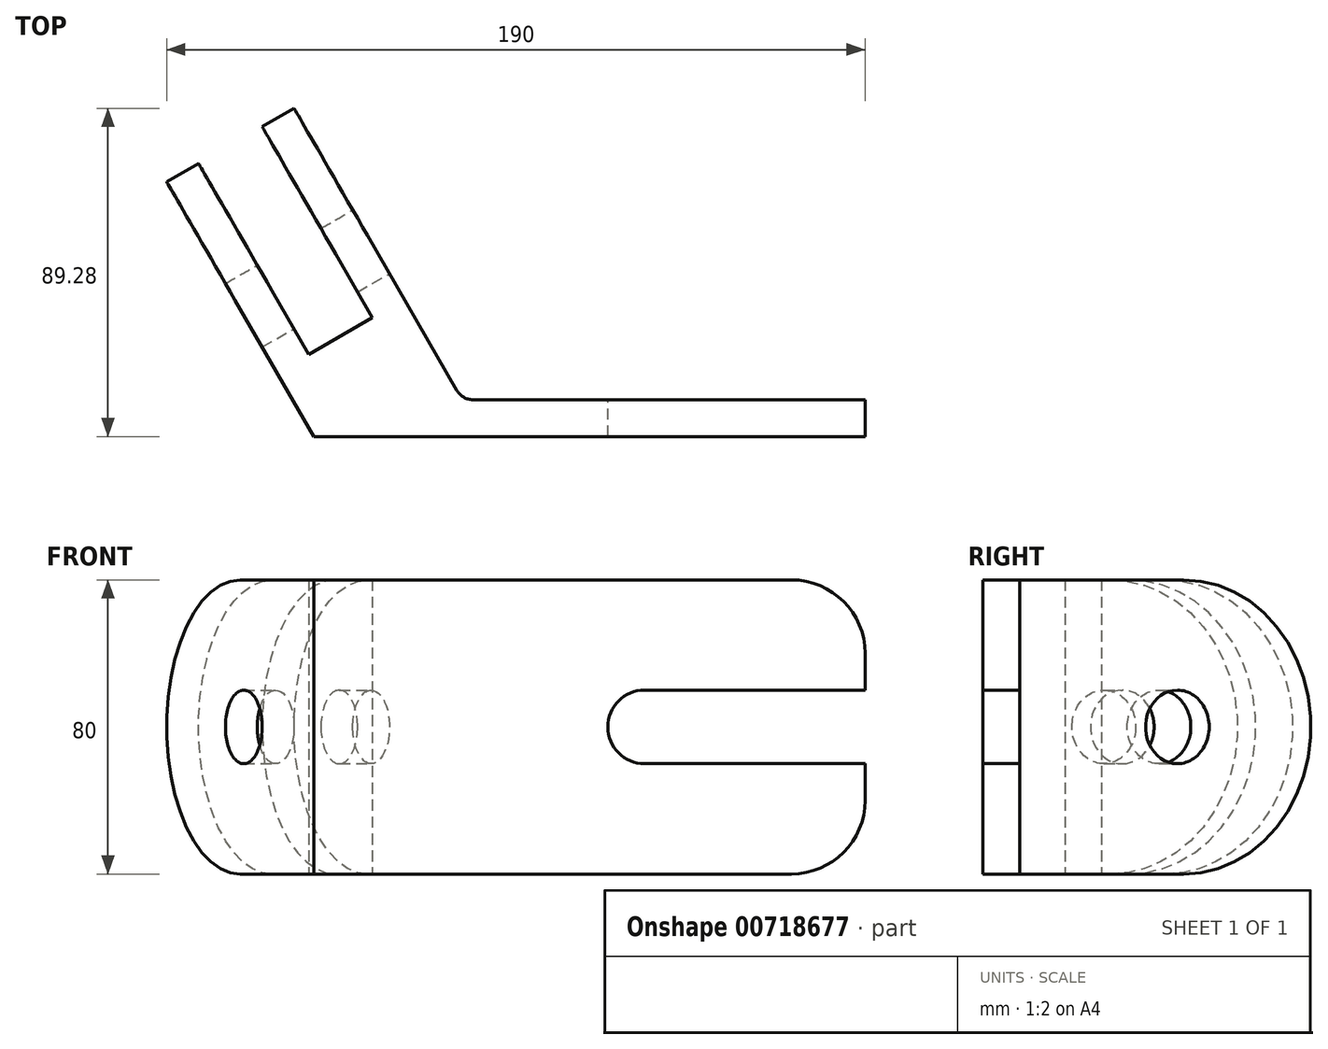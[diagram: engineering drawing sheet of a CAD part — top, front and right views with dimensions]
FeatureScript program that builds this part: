
annotation { "Feature Type Name" : "Feature", "Feature Type Description" : "" }
export const myFeature = defineFeature(function(context is Context, id is Id, definition is map)
    precondition{}
    {
        {
            var Q0;
            Q0=qCreatedBy(makeId("Top.planeOp"),FACE);
            var sketch = newSketch(context, id + "F0", { "sketchPlane" : qUnion([Q0])});
            skLineSegment(sketch, "E0", {"start": v(105.59, 0) * mm, "end": v(-44.41, 0) * mm});
            skLineSegment(sketch, "E1", {"start": v(-44.41, 0) * mm, "end": v(-84.41, 69.28) * mm});
            skLineSegment(sketch, "E2", {"start": v(-49.77, 89.28) * mm, "end": v(-4, 10) * mm});
            skLineSegment(sketch, "E3", {"start": v(-4, 10) * mm, "end": v(105.59, 10) * mm});
            skLineSegment(sketch, "E4", {"start": v(105.59, 10) * mm, "end": v(105.59, 0) * mm});
            skLineSegment(sketch, "E5", {"start": v(-84.41, 69.28) * mm, "end": v(-75.75, 74.28) * mm});
            skLineSegment(sketch, "E6", {"start": v(-75.75, 74.28) * mm, "end": v(-45.75, 22.32) * mm});
            skLineSegment(sketch, "E7", {"start": v(-45.75, 22.32) * mm, "end": v(-28.43, 32.32) * mm});
            skLineSegment(sketch, "E8", {"start": v(-28.43, 32.32) * mm, "end": v(-58.43, 84.28) * mm});
            skLineSegment(sketch, "E9", {"start": v(-58.43, 84.28) * mm, "end": v(-49.77, 89.28) * mm});
            skSolve(sketch);
        }
        {
            var Q0;
            Q0=makeQuery(id+"F0.imprint","IMPRINT",FACE,{"disambiguationData":[TD([[makeQuery(id+"F0.imprint","IMPRINT",EDGE,{"derivedFrom":sQuery(id+"F0.wireOp",EDGE,"E0")}),-1.0]])]});
            extrude(context, id + "F1", {"entities" : qUnion([Q0]), "depth" : 40 * mm, "offsetDistance" : 25 * mm, "hasSecondDirection" : true, "secondDirectionOppositeDirection" : true, "secondDirectionDepth" : 40 * mm});
        }
        {
            var Q0;
            Q0=makeQuery(id+"F1.opExtrude","SWEPT_EDGE",EDGE,{"disambiguationData":[OSD([sQuery(id+"F0.wireOp",EDGE,"E2"),sQuery(id+"F0.wireOp",EDGE,"E3")])]});
            fillet(context, id + "F2", {"entities" : qUnion([Q0]), "radius" : 5 * mm, "tangentPropagation" : true, "allowEdgeOverflow" : false});
        }
        {
            var Q0;
            Q0=makeQuery(id+"F1.opExtrude","CAP_EDGE",EDGE,{"disambiguationData":[OSD([sQuery(id+"F0.wireOp",EDGE,"E9")])],"isStart":false});
            var Q1;
            Q1=makeQuery(id+"F1.opExtrude","CAP_EDGE",EDGE,{"disambiguationData":[OSD([sQuery(id+"F0.wireOp",EDGE,"E5")])],"isStart":false});
            var Q2;
            Q2=makeQuery(id+"F1.opExtrude","CAP_EDGE",EDGE,{"disambiguationData":[OSD([sQuery(id+"F0.wireOp",EDGE,"E5")])],"isStart":true});
            var Q3;
            Q3=makeQuery(id+"F1.opExtrude","CAP_EDGE",EDGE,{"disambiguationData":[OSD([sQuery(id+"F0.wireOp",EDGE,"E9")])],"isStart":true});
            fillet(context, id + "F3", {"entities" : qUnion([Q0, Q1, Q2, Q3]), "radius" : 40 * mm, "tangentPropagation" : true, "allowEdgeOverflow" : false});
        }
        {
            var Q0;
            Q0=makeQuery(id+"F1.opExtrude","SWEPT_FACE",FACE,{"disambiguationData":[OSD([sQuery(id+"F0.wireOp",EDGE,"E2")])]});
            var sketch = newSketch(context, id + "F4", { "sketchPlane" : qUnion([Q0])});
            skLineSegment(sketch, "E10", {"start": v(13.55, 0) * mm, "end": v(60.25, 0) * mm, "construction": true});
            skCircle(sketch, "E11", {"center": v(60.25, 0) * mm, "radius": 10 * mm});
            skSolve(sketch);
        }
        {
            var Q0;
            Q0=makeQuery(id+"F4.imprint","IMPRINT",FACE,{"disambiguationData":[TD([[makeQuery(id+"F4.imprint","IMPRINT",EDGE,{"derivedFrom":sQuery(id+"F4.wireOp",EDGE,"E11")}),1.0]])]});
            extrude(context, id + "F5", {"entities" : qUnion([Q0]), "operationType" : NewBodyOperationType.REMOVE, "oppositeDirection" : true, "depth" : 52.2 * mm, "offsetDistance" : 25 * mm});
        }
        {
            var Q0;
            Q0=makeQuery(id+"F1.opExtrude","SWEPT_FACE",FACE,{"disambiguationData":[OSD([sQuery(id+"F0.wireOp",EDGE,"E3")])]});
            var sketch = newSketch(context, id + "F6", { "sketchPlane" : qUnion([Q0])});
            skCircle(sketch, "E12", {"center": v(-45.59, 0) * mm, "radius": 10 * mm});
            skLineSegment(sketch, "E13", {"start": v(-45.59, -10) * mm, "end": v(-105.59, -10) * mm});
            skLineSegment(sketch, "E14.MirrorCS", {"start": v(-45.59, 10) * mm, "end": v(-105.59, 10) * mm});
            skLineSegment(sketch, "E15", {"start": v(-105.59, 10) * mm, "end": v(-105.59, -10) * mm});
            skSolve(sketch);
        }
        {
            var Q0;
            {var subQ0=sQuery(id+"F6.wireOp",EDGE,"E13");Q0=makeQuery(id+"F6.imprint","IMPRINT",FACE,{"disambiguationData":[TD([[makeQuery(id+"F6.imprint","IMPRINT",EDGE,{"derivedFrom":subQ0}),-1.0]])]});}
            var Q1;
            {var subQ0=sQuery(id+"F6.wireOp",EDGE,"E12");var subQ1=makeQuery(id+"F6.imprint","INTERSECT",VERTEX,{"derivedFrom":[subQ0,sQuery(id+"F6.wireOp",EDGE,"E13")]});Q1=makeQuery(id+"F6.imprint","IMPRINT",FACE,{"disambiguationData":[TD([[makeQuery(id+"F6.imprint","IMPRINT",EDGE,{"disambiguationData":[TD([[subQ1,1.0]])],"derivedFrom":subQ0}),1.0]])]});}
            extrude(context, id + "F7", {"entities" : qUnion([Q0, Q1]), "operationType" : NewBodyOperationType.REMOVE, "oppositeDirection" : true, "depth" : 25 * mm, "offsetDistance" : 25 * mm});
        }
        {
            var Q0;
            Q0=makeQuery(id+"F1.opExtrude","CAP_EDGE",EDGE,{"disambiguationData":[OSD([sQuery(id+"F0.wireOp",EDGE,"E4")])],"isStart":true});
            var Q1;
            Q1=makeQuery(id+"F1.opExtrude","CAP_EDGE",EDGE,{"disambiguationData":[OSD([sQuery(id+"F0.wireOp",EDGE,"E4")])],"isStart":false});
            fillet(context, id + "F8", {"entities" : qUnion([Q0, Q1]), "radius" : 20 * mm, "tangentPropagation" : true, "allowEdgeOverflow" : false});
        }
    });
